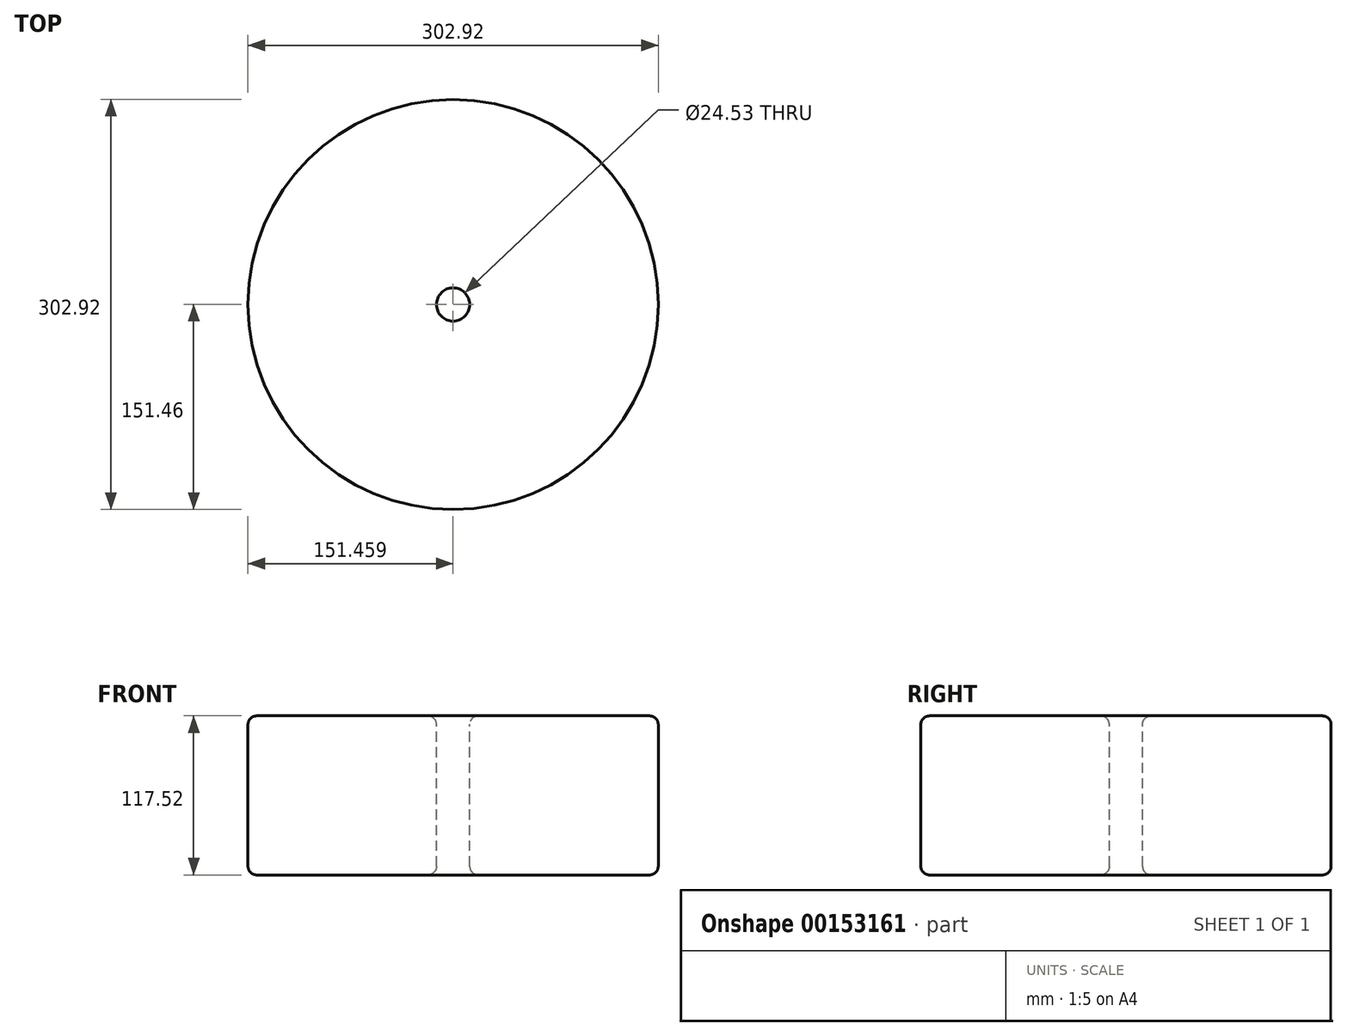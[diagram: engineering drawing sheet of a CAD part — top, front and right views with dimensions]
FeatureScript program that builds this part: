
annotation { "Feature Type Name" : "Feature", "Feature Type Description" : "" }
export const myFeature = defineFeature(function(context is Context, id is Id, definition is map)
    precondition{}
    {
        {
            var Q0;
            Q0=qCreatedBy(makeId("Front.planeOp"),FACE);
            var sketch = newSketch(context, id + "F0", { "sketchPlane" : qUnion([Q0])});
            skLineSegment(sketch, "E0.bottom", {"start": v(-66.81, 46.92) * mm, "end": v(59.68, 46.92) * mm});
            skLineSegment(sketch, "E0.top", {"start": v(-66.81, -70.6) * mm, "end": v(59.68, -70.6) * mm});
            skLineSegment(sketch, "E0.left", {"start": v(-73.16, 40.57) * mm, "end": v(-73.16, -64.25) * mm});
            skLineSegment(sketch, "E0.right", {"start": v(66.03, 40.57) * mm, "end": v(66.03, -64.25) * mm});
            skLineSegment(sketch, "E1", {"start": v(78.3, 58.9) * mm, "end": v(78.3, -78.01) * mm, "construction": true});
            skPoint(sketch, "E2.visualSharp", {"position": v(-73.16, 46.92) * mm});
            skArc(sketch, "E2.filletArc", {"start": v(-66.81, 46.92) * mm, "mid": v(-71.3, 45.06) * mm, "end": v(-73.16, 40.57) * mm});
            skPoint(sketch, "E3.visualSharp", {"position": v(-73.16, -70.6) * mm});
            skArc(sketch, "E3.filletArc", {"start": v(-73.16, -64.25) * mm, "mid": v(-71.3, -68.74) * mm, "end": v(-66.81, -70.6) * mm});
            skPoint(sketch, "E4.visualSharp", {"position": v(66.03, -70.6) * mm});
            skArc(sketch, "E4.filletArc", {"start": v(59.68, -70.6) * mm, "mid": v(64.17, -68.74) * mm, "end": v(66.03, -64.25) * mm});
            skPoint(sketch, "E5.visualSharp", {"position": v(66.03, 46.92) * mm});
            skArc(sketch, "E5.filletArc", {"start": v(66.03, 40.57) * mm, "mid": v(64.17, 45.06) * mm, "end": v(59.68, 46.92) * mm});
            skSolve(sketch);
        }
        {
            var Q0;
            Q0=makeQuery(id+"F0.imprint","IMPRINT",FACE,{"disambiguationData":[TD([[makeQuery(id+"F0.imprint","IMPRINT",EDGE,{"derivedFrom":sQuery(id+"F0.wireOp",EDGE,"E0.bottom")}),-1.0]])]});
            var Q1;
            Q1=sQuery(id+"F0.wireOp",EDGE,"E1");
            revolve(context, id + "F1", {"entities" : qUnion([Q0]), "axis" : qUnion([Q1]), "revolveType" : RevolveType.FULL});
        }
    });
